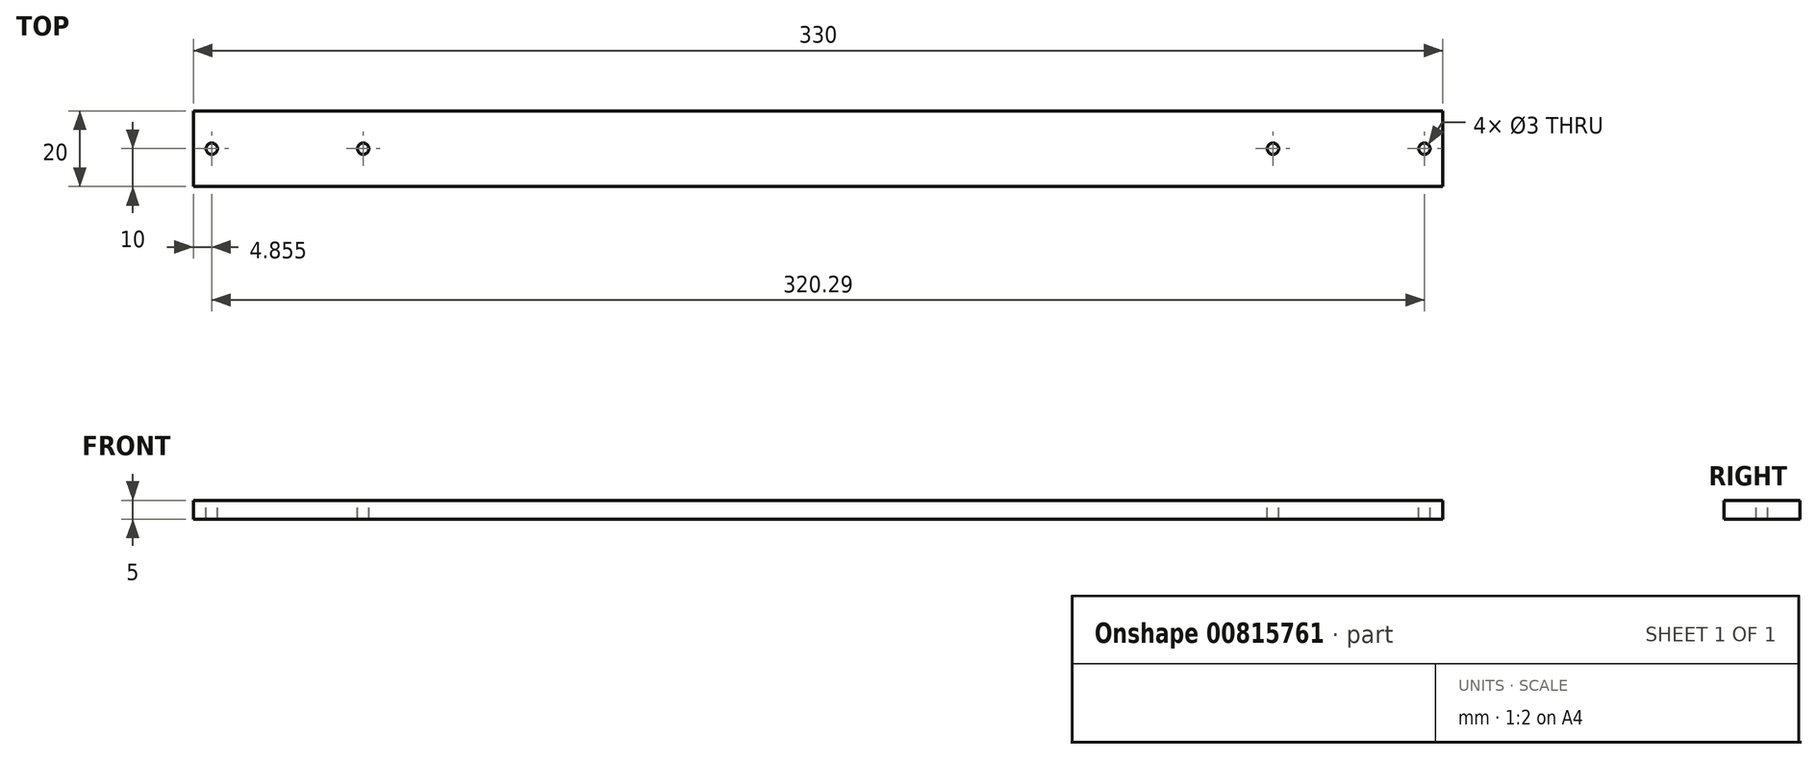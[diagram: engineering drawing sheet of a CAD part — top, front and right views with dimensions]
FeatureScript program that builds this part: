
annotation { "Feature Type Name" : "Feature", "Feature Type Description" : "" }
export const myFeature = defineFeature(function(context is Context, id is Id, definition is map)
    precondition{}
    {
        {
            var Q0;
            Q0=qCreatedBy(makeId("Top.planeOp"),FACE);
            var sketch = newSketch(context, id + "F0", { "sketchPlane" : qUnion([Q0])});
            skLineSegment(sketch, "E0.bottom", {"start": v(160.15, 0) * mm, "end": v(-160.15, 0) * mm});
            skLineSegment(sketch, "E0.top", {"start": v(160.15, 0) * mm, "end": v(-160.15, 0) * mm});
            skLineSegment(sketch, "E0.left", {"start": v(-160.14, 0) * mm, "end": v(-160.14, 0) * mm});
            skLineSegment(sketch, "E0.right", {"start": v(160.15, 0) * mm, "end": v(160.15, 0) * mm});
            skPoint(sketch, "E0.middle", {"position": v(0, 0) * mm});
            skLineSegment(sketch, "E1.bottom", {"start": v(165, -10) * mm, "end": v(-165, -10) * mm});
            skLineSegment(sketch, "E1.top", {"start": v(165, 10) * mm, "end": v(-165, 10) * mm});
            skLineSegment(sketch, "E1.left", {"start": v(165, -10) * mm, "end": v(165, 10) * mm});
            skLineSegment(sketch, "E1.right", {"start": v(-165, -10) * mm, "end": v(-165, 10) * mm});
            skPoint(sketch, "E2", {"position": v(-160.15, 0) * mm});
            skPoint(sketch, "E3", {"position": v(160.15, 0) * mm});
            skLineSegment(sketch, "E4.bottom", {"start": v(120.14, 0) * mm, "end": v(-120.14, 0) * mm});
            skLineSegment(sketch, "E4.top", {"start": v(120.14, 0) * mm, "end": v(-120.14, 0) * mm});
            skLineSegment(sketch, "E4.left", {"start": v(120.14, 0) * mm, "end": v(120.14, 0) * mm});
            skLineSegment(sketch, "E4.right", {"start": v(-120.14, 0) * mm, "end": v(-120.14, 0) * mm});
            skPoint(sketch, "E5", {"position": v(-120.14, 0) * mm});
            skPoint(sketch, "E6", {"position": v(120.14, 0) * mm});
            skSolve(sketch);
        }
        {
            var Q0;
            Q0 = qSketchRegion(id + "F0", true);
            extrude(context, id + "F1", {"entities" : qUnion([Q0]), "oppositeDirection" : true, "depth" : 5 * mm, "offsetDistance" : 25 * mm});
        }
        {
            var Q0;
            Q0=sQuery(id+"F0.wireOp",VERTEX,"E2");
            var Q1;
            Q1=sQuery(id+"F0.wireOp",VERTEX,"E3");
            var Q2;
            Q2=makeQuery(id+"F1.opExtrude","SWEPT_BODY",BODY,{"disambiguationData":[OSD([sQuery(id+"F0.wireOp",EDGE,"E1.bottom"),sQuery(id+"F0.wireOp",EDGE,"E1.top"),sQuery(id+"F0.wireOp",EDGE,"E1.left"),sQuery(id+"F0.wireOp",EDGE,"E1.right")])]});
            hole(context, id + "F2", {"style" : HoleStyle.SIMPLE, "endStyle" : HoleEndStyle.THROUGH, "holeDiameter" : 3 * mm, "majorDiameter" : 5 * mm, "isTappedThrough" : true, "tappedDepth" : 12 * mm, "tapClearance" : 3, "locations" : qUnion([Q0, Q1]), "scope" : qUnion([Q2])});
        }
        {
            var Q0;
            Q0=sQuery(id+"F0.wireOp",VERTEX,"E5");
            var Q1;
            Q1=sQuery(id+"F0.wireOp",VERTEX,"E6");
            var Q2;
            Q2=makeQuery(id+"F1.opExtrude","SWEPT_BODY",BODY,{"disambiguationData":[OSD([sQuery(id+"F0.wireOp",EDGE,"E1.bottom"),sQuery(id+"F0.wireOp",EDGE,"E1.top"),sQuery(id+"F0.wireOp",EDGE,"E1.left"),sQuery(id+"F0.wireOp",EDGE,"E1.right")])]});
            hole(context, id + "F3", {"style" : HoleStyle.SIMPLE, "endStyle" : HoleEndStyle.THROUGH, "holeDiameter" : 3 * mm, "majorDiameter" : 5 * mm, "isTappedThrough" : true, "tappedDepth" : 12 * mm, "tapClearance" : 3, "locations" : qUnion([Q0, Q1]), "scope" : qUnion([Q2])});
        }
    });
